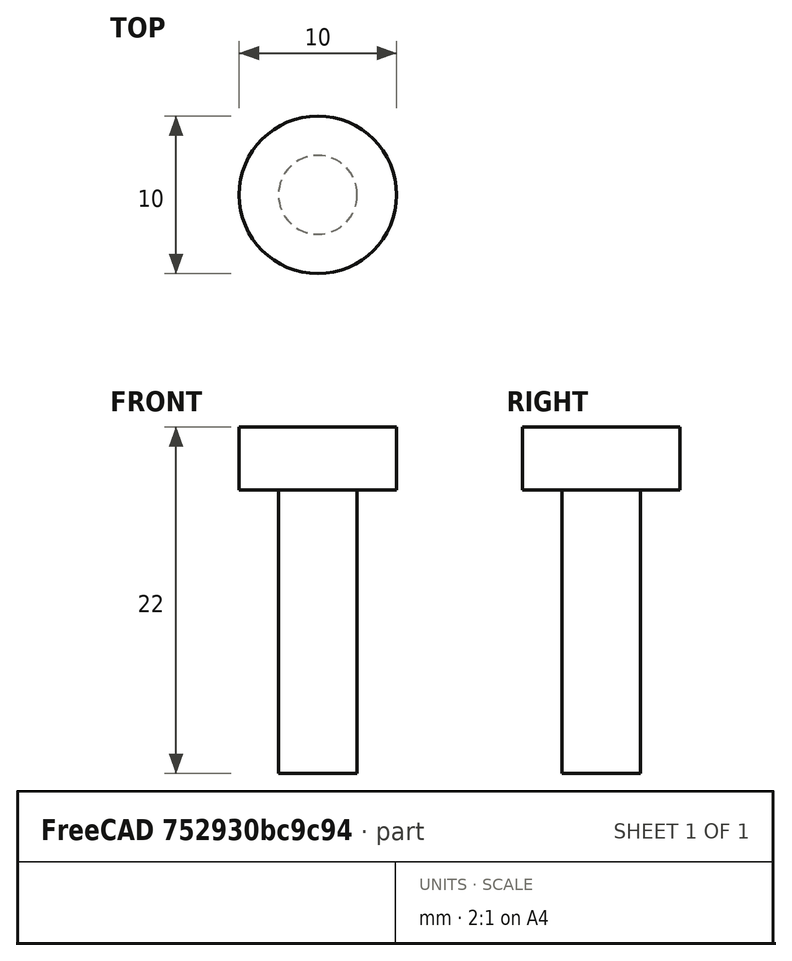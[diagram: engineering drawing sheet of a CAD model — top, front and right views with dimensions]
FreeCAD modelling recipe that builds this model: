
FCSTD DOCUMENT  (FreeCAD 0.19R)
Label: Mutter M4X13 5X20
License: All rights reserved
LicenseURL: http://en.wikipedia.org/wiki/All_rights_reserved
objects: Sketcher::SketchObject×1, PartDesign::Revolution×1, PartDesign::Body×1
note: 4 computed .brp shape members not serialized (recipe doc carries the construction recipe); baked Part::Feature solids carry a one-line shape summary decoded from their .brp

FEATURE [Sketcher::SketchObject] Sketch
  FullyConstrained = true
  MapMode = 5
  Placement = pos=(0,0,0) rot=(1,0,0;1.5708rad)
  Support = -> [XZ_Plane]
  sketch-geometry (6):
    g0: LineSegment StartX=0 StartY=-1e-16 StartZ=0 EndX=5 EndY=-1e-16 EndZ=0
    g1: LineSegment StartX=5 StartY=-1e-16 StartZ=0 EndX=5 EndY=-4 EndZ=0
    g2: LineSegment StartX=5 StartY=-4 StartZ=0 EndX=2.5 EndY=-4 EndZ=0
    g3: LineSegment StartX=2.5 StartY=-4 StartZ=0 EndX=2.5 EndY=-22 EndZ=0
    g4: LineSegment StartX=2.5 StartY=-22 StartZ=0 EndX=0 EndY=-22 EndZ=0
    g5: LineSegment StartX=0 StartY=-22 StartZ=0 EndX=0 EndY=0 EndZ=0
  constraints (17):
    c: Horizontal(g0)
    c: Coincident(g0,g1)
    c: Vertical(g1)
    c: Coincident(g1,g2)
    c: Horizontal(g2)
    c: Coincident(g2,g3)
    c: Vertical(g3)
    c: Coincident(g3,g4)
    c: PointOnObject(g4,g-2)
    c: Horizontal(g4)
    c: Coincident(g4,g5)
    c: Coincident(g5,g0)
    c: Distance(g4) = 2.5
    c: Distance(g3) = 18
    c: Distance(g1) = 4
    c: Distance(g0) = 5
    c: Coincident(g0,g-1)
FEATURE [PartDesign::Revolution] Revolution
  Angle = 360
  Axis = (0,2e-16,1)
  Base = (0,0,0)
  Placement = pos=(0,0,0) rot=(1,0,0;1.5708rad)
  Profile = -> Sketch
  ReferenceAxis = -> Sketch [V_Axis]
  Reversed = true
FEATURE [PartDesign::Body] Body
  Group = -> [Sketch,Revolution]
  Origin = -> Origin
  Tip = -> Revolution
